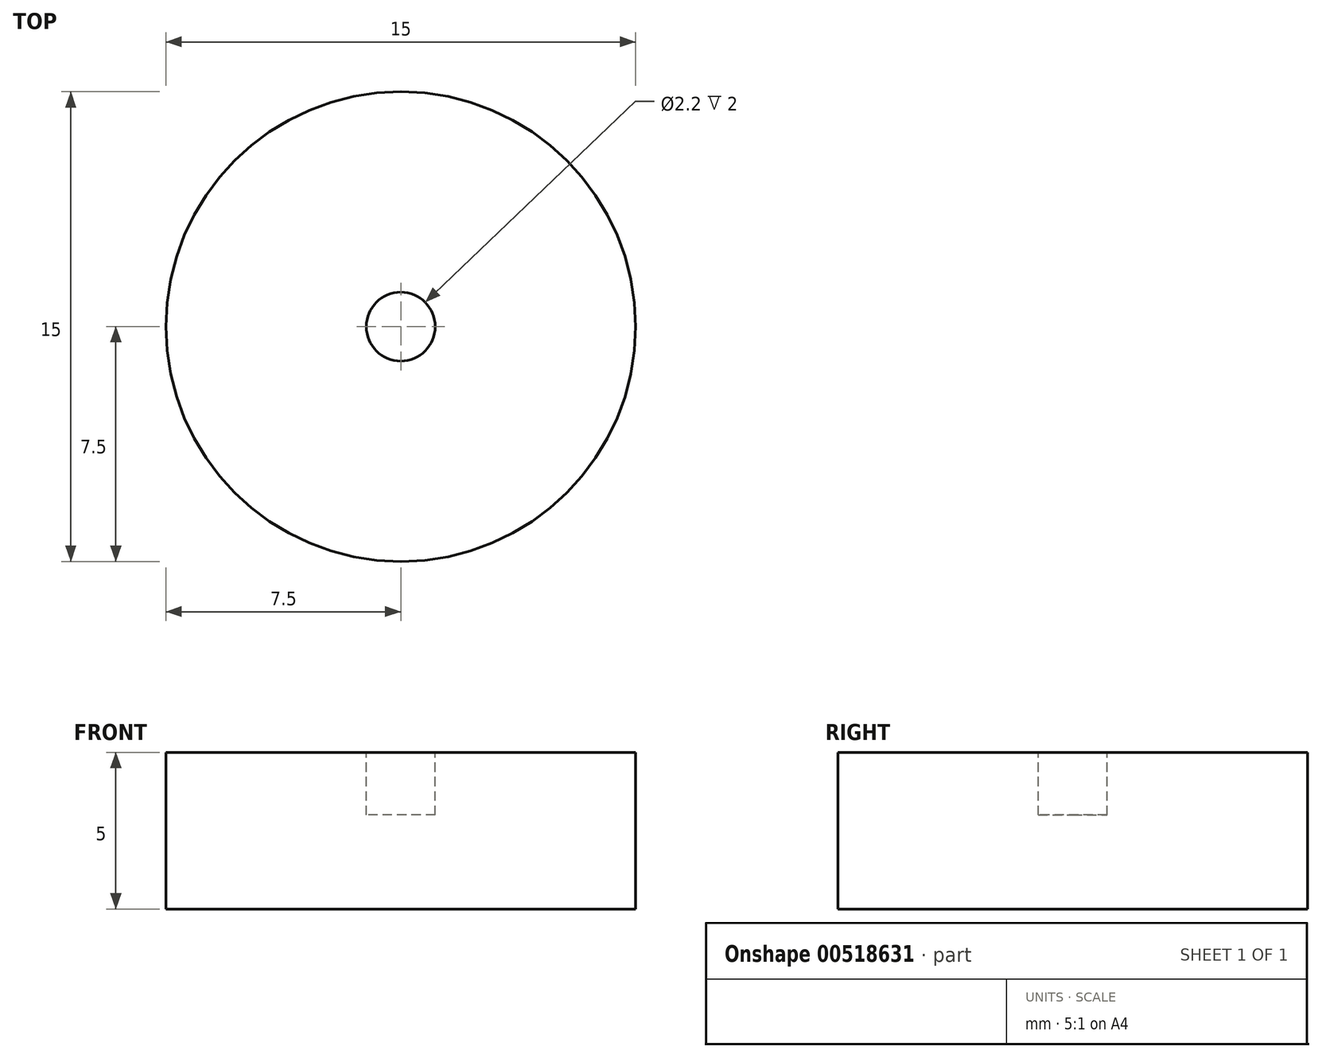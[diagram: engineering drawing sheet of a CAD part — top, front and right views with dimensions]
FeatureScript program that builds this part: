
annotation { "Feature Type Name" : "Feature", "Feature Type Description" : "" }
export const myFeature = defineFeature(function(context is Context, id is Id, definition is map)
    precondition{}
    {
        {
            var Q0;
            Q0=qCreatedBy(makeId("Top.planeOp"),FACE);
            var sketch = newSketch(context, id + "F0", { "sketchPlane" : qUnion([Q0])});
            skCircle(sketch, "E0", {"center": v(0, 0) * mm, "radius": 7.5 * mm});
            skSolve(sketch);
        }
        {
            var Q0;
            Q0 = qSketchRegion(id + "F0", true);
            extrude(context, id + "F1", {"entities" : qUnion([Q0]), "depth" : 5 * mm, "offsetDistance" : 25 * mm});
        }
        {
            var Q0;
            Q0=makeQuery(id+"F1.opExtrude","CAP_FACE",FACE,{"disambiguationData":[OSD([sQuery(id+"F0.wireOp",EDGE,"E0")])],"isStart":false});
            var sketch = newSketch(context, id + "F2", { "sketchPlane" : qUnion([Q0])});
            skCircle(sketch, "E1", {"center": v(0, 0) * mm, "radius": 1.1 * mm});
            skSolve(sketch);
        }
        {
            var Q0;
            Q0 = qSketchRegion(id + "F2", true);
            var Q1;
            Q1=sQuery(id+"F2.wireOp",EDGE,"E1");
            extrude(context, id + "F3", {"entities" : qUnion([Q0]), "operationType" : NewBodyOperationType.REMOVE, "surfaceEntities" : qUnion([Q1]), "oppositeDirection" : true, "depth" : 2 * mm, "offsetDistance" : 25 * mm});
        }
    });
